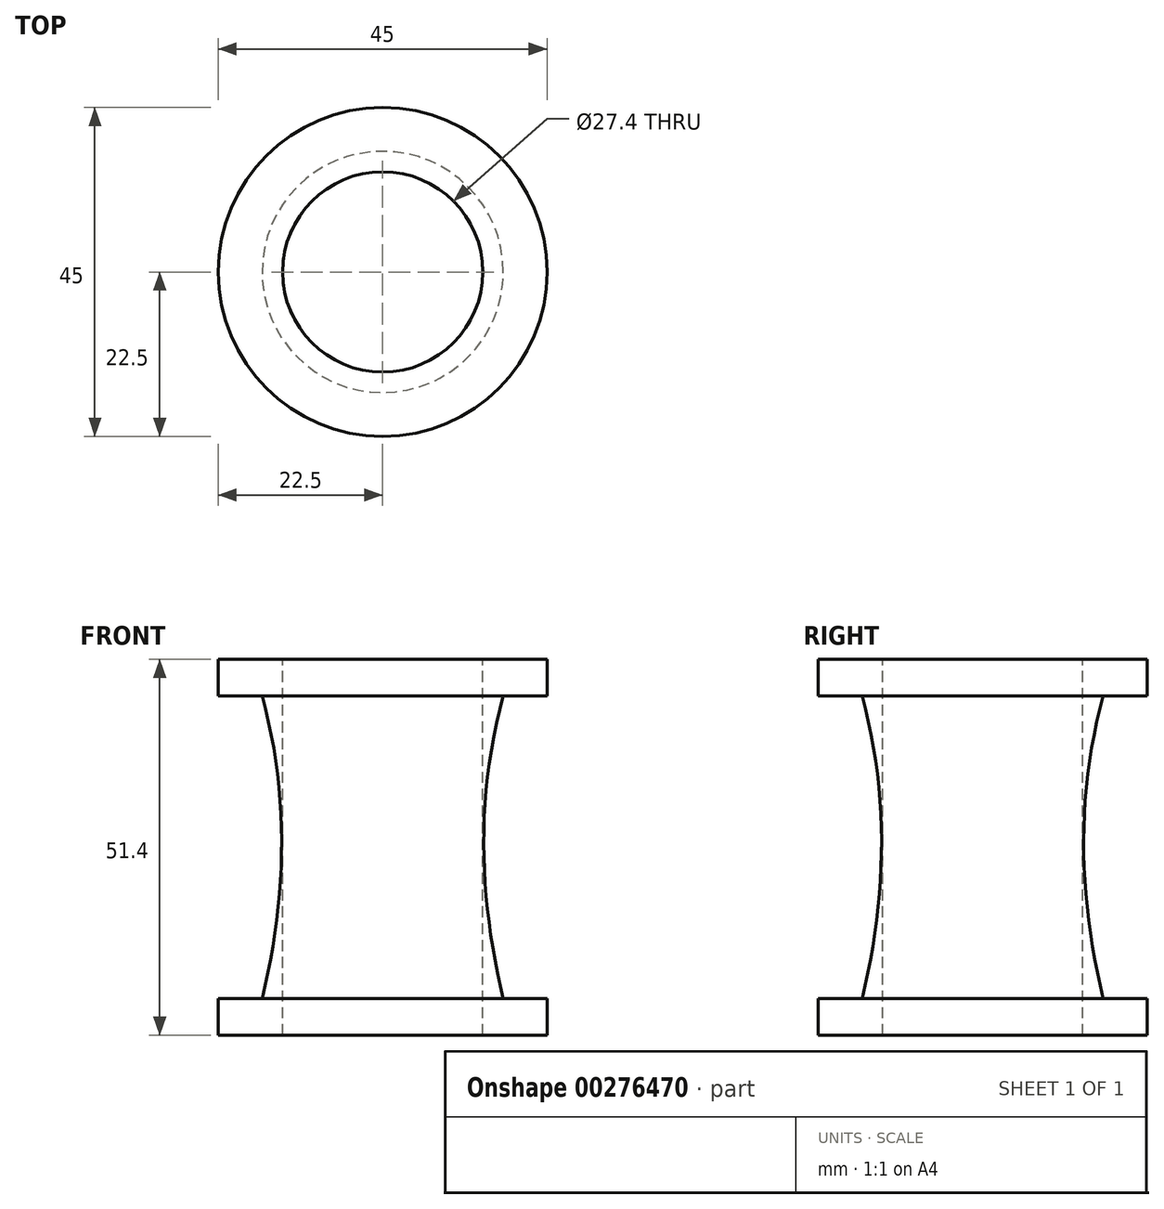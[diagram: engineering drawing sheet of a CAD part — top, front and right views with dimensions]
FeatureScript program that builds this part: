
annotation { "Feature Type Name" : "Feature", "Feature Type Description" : "" }
export const myFeature = defineFeature(function(context is Context, id is Id, definition is map)
    precondition{}
    {
        {
            var Q0;
            Q0=qCreatedBy(makeId("Front.planeOp"),FACE);
            var sketch = newSketch(context, id + "F0", { "sketchPlane" : qUnion([Q0])});
            skLineSegment(sketch, "E0", {"start": v(0, 0) * mm, "end": v(0, -25.7) * mm});
            skLineSegment(sketch, "E1", {"start": v(0, -25.7) * mm, "end": v(-22.5, -25.7) * mm});
            skLineSegment(sketch, "E2", {"start": v(-22.5, -25.7) * mm, "end": v(-22.5, -20.7) * mm});
            skLineSegment(sketch, "E3", {"start": v(-22.5, 25.7) * mm, "end": v(-22.5, 20.7) * mm});
            skLineSegment(sketch, "E4", {"start": v(-22.5, 25.7) * mm, "end": v(0, 25.7) * mm});
            skLineSegment(sketch, "E5", {"start": v(0, 25.7) * mm, "end": v(0, 0) * mm});
            skLineSegment(sketch, "E6", {"start": v(-16.5, -20.7) * mm, "end": v(-22.5, -20.7) * mm});
            skLineSegment(sketch, "E7", {"start": v(-16.5, 20.7) * mm, "end": v(-22.5, 20.7) * mm});
            skFitSpline(sketch, "E8", {"points": [v(-16.5, 20.7) * mm, v(-16.5, -20.7) * mm], "startDerivative": vector(11.73, -42.81) * mm, "endDerivative": vector(-9.59, -39.6) * mm});
            skSolve(sketch);
        }
        {
            var Q0;
            Q0=makeQuery(id+"F0.imprint","IMPRINT",FACE,{"disambiguationData":[TD([[makeQuery(id+"F0.imprint","IMPRINT",EDGE,{"derivedFrom":sQuery(id+"F0.wireOp",EDGE,"E0")}),-1.0]])]});
            var Q1;
            Q1=sQuery(id+"F0.wireOp",EDGE,"E0");
            revolve(context, id + "F1", {"entities" : qUnion([Q0]), "axis" : qUnion([Q1]), "revolveType" : RevolveType.FULL});
        }
        {
            var Q0;
            Q0=makeQuery(id+"F1.opRevolve","SWEPT_FACE",FACE,{"disambiguationData":[OSD([sQuery(id+"F0.wireOp",EDGE,"E4")])]});
            var sketch = newSketch(context, id + "F2", { "sketchPlane" : qUnion([Q0])});
            skCircle(sketch, "E9", {"center": v(0, 0) * mm, "radius": 13.7 * mm});
            skSolve(sketch);
        }
        {
            var Q0;
            Q0 = qSketchRegion(id + "F2", true);
            var Q1;
            Q1=makeQuery(id+"F1.opRevolve","SWEPT_FACE",FACE,{"disambiguationData":[OSD([sQuery(id+"F0.wireOp",EDGE,"E1")])]});
            extrude(context, id + "F3", {"entities" : qUnion([Q0]), "operationType" : NewBodyOperationType.REMOVE, "endBound" : BoundingType.UP_TO_SURFACE, "oppositeDirection" : true, "endBoundEntityFace" : qUnion([Q1]), "depth" : 53.3 * mm});
        }
    });
